FCSTD DOCUMENT  (FreeCAD 1.0R38643 (Git))
Label: Acryl03
License: All rights reserved
LicenseURL: https://en.wikipedia.org/wiki/All_rights_reserved
objects: Sketcher::SketchObject×1, PartDesign::Body×1
note: 3 computed .brp shape members not serialized (recipe doc carries the construction recipe); baked Part::Feature solids carry a one-line shape summary decoded from their .brp

FEATURE [Sketcher::SketchObject] Sketch
  ArcFitTolerance = 1e-06
  AttachmentSupport = -> [XY_Plane]
  FullyConstrained = false
  MakeInternals = false
  MapMode = 5
  sketch-geometry (64):
    g0: LineSegment StartX=-152.327 StartY=63 StartZ=0 EndX=-152.327 EndY=44.1 EndZ=0
    g1: LineSegment StartX=-140.327 StartY=3.12586e-11 StartZ=0 EndX=-108.827 EndY=3.12586e-11 EndZ=0
    g2: LineSegment StartX=5.67322 StartY=74.9996 StartZ=0 EndX=-25.8266 EndY=74.9996 EndZ=0
    g3: ArcOfCircle CenterX=-140.327 CenterY=63 CenterZ=0 NormalX=0 NormalY=0 NormalZ=1 AngleXU=0 Radius=12 StartAngle=1.5708 EndAngle=3.14159
    g4: ArcOfCircle CenterX=-140.327 CenterY=12 CenterZ=0 NormalX=0 NormalY=0 NormalZ=1 AngleXU=0 Radius=12 StartAngle=3.14159 EndAngle=4.71239
    g5: ArcOfCircle CenterX=5.85959 CenterY=12 CenterZ=0 NormalX=0 NormalY=0 NormalZ=1 AngleXU=0 Radius=12 StartAngle=4.71242 EndAngle=6.28319
    g6: ArcOfCircle CenterX=5.67322 CenterY=62.9996 CenterZ=0 NormalX=0 NormalY=0 NormalZ=1 AngleXU=0 Radius=12 StartAngle=3.18953e-05 EndAngle=1.5708
    g7: GeomPoint [constr] X=-152.327 Y=75 Z=0
    g8: GeomPoint [constr] X=17.8605 Y=0 Z=0
    g9: Circle CenterX=5.96219 CenterY=55.25 CenterZ=0 NormalX=0 NormalY=0 NormalZ=1 AngleXU=0 Radius=1.1
    g10: Circle CenterX=-65.0378 CenterY=55.25 CenterZ=0 NormalX=0 NormalY=0 NormalZ=1 AngleXU=0 Radius=1.1
    g11: Circle CenterX=-65.0378 CenterY=19.75 CenterZ=0 NormalX=0 NormalY=0 NormalZ=1 AngleXU=0 Radius=1.1
    g12: Circle CenterX=5.96219 CenterY=19.75 CenterZ=0 NormalX=0 NormalY=0 NormalZ=1 AngleXU=0 Radius=1.1
    g13: ArcOfCircle CenterX=-12.1395 CenterY=37.5 CenterZ=0 NormalX=0 NormalY=0 NormalZ=1 AngleXU=0 Radius=12 StartAngle=1.5708 EndAngle=4.71239
    g14: LineSegment StartX=17.8605 StartY=25.5 StartZ=0 EndX=-12.1395 EndY=25.5 EndZ=0
    g15: LineSegment StartX=17.8605 StartY=49.5 StartZ=0 EndX=-12.1395 EndY=49.5 EndZ=0
    g16: LineSegment [constr] StartX=-65.0378 StartY=55.25 StartZ=0 EndX=-65.0378 EndY=19.75 EndZ=0
    g17: GeomPoint X=17.8605 Y=49.5 Z=0
    g18: GeomPoint X=17.8605 Y=25.5 Z=0
    g19: LineSegment StartX=17.8605 StartY=25.5 StartZ=0 EndX=17.8605 EndY=12 EndZ=0
    g20: LineSegment StartX=17.8605 StartY=49.5 StartZ=0 EndX=17.8605 EndY=63 EndZ=0
    g21: Circle CenterX=-140.327 CenterY=63 CenterZ=0 NormalX=0 NormalY=0 NormalZ=1 AngleXU=0 Radius=1.1
    g22: Circle CenterX=-140.327 CenterY=12 CenterZ=0 NormalX=0 NormalY=0 NormalZ=1 AngleXU=0 Radius=1.1
    g23: Circle CenterX=5.85959 CenterY=12 CenterZ=0 NormalX=0 NormalY=0 NormalZ=1 AngleXU=0 Radius=1.1
    g24: Circle CenterX=5.67322 CenterY=62.9996 CenterZ=0 NormalX=0 NormalY=0 NormalZ=1 AngleXU=0 Radius=1.1
    g25: LineSegment [constr] StartX=-115.261 StartY=75 StartZ=0 EndX=-115.261 EndY=4.69e-13 EndZ=0
    g26: GeomPoint X=-115.261 Y=37.5 Z=0
    g27: Circle CenterX=-115.261 CenterY=37.5 CenterZ=0 NormalX=0 NormalY=0 NormalZ=1 AngleXU=0 Radius=3.75
    g28: Circle CenterX=-115.261 CenterY=56.25 CenterZ=0 NormalX=0 NormalY=0 NormalZ=1 AngleXU=0 Radius=3.75
    g29: LineSegment [constr] StartX=-110.295 StartY=75 StartZ=0 EndX=-110.295 EndY=37.5 EndZ=0
    g30: GeomPoint X=-110.295 Y=56.25 Z=0
    g31: LineSegment [constr] StartX=-110.295 StartY=56.25 StartZ=0 EndX=-152.327 EndY=56.25 EndZ=0
    g32: GeomPoint X=-115.261 Y=56.25 Z=0
    g33: Circle CenterX=-115.261 CenterY=18.75 CenterZ=0 NormalX=0 NormalY=0 NormalZ=1 AngleXU=0 Radius=3.75
    g34: GeomPoint X=-115.261 Y=18.75 Z=0
    g35: LineSegment StartX=-108.827 StartY=71 StartZ=0 EndX=-98.8266 EndY=71 EndZ=0
    g36: LineSegment StartX=-72.3266 StartY=71 StartZ=0 EndX=-62.3266 EndY=71 EndZ=0
    g37: LineSegment StartX=-62.3266 StartY=71 StartZ=0 EndX=-62.3266 EndY=75 EndZ=0
    g38: LineSegment StartX=-72.3266 StartY=75 StartZ=0 EndX=-72.3266 EndY=71 EndZ=0
    g39: LineSegment StartX=-35.8266 StartY=71 StartZ=0 EndX=-25.8266 EndY=71 EndZ=0
    g40: LineSegment StartX=-25.8266 StartY=71 StartZ=0 EndX=-25.8266 EndY=74.9996 EndZ=0
    g41: LineSegment StartX=-35.8266 StartY=75 StartZ=0 EndX=-35.8266 EndY=71 EndZ=0
    g42: GeomPoint X=-108.827 Y=75 Z=0
    g43: LineSegment StartX=-108.827 StartY=75 StartZ=0 EndX=-108.827 EndY=71 EndZ=0
    g44: LineSegment StartX=-98.8266 StartY=71 StartZ=0 EndX=-98.8266 EndY=75 EndZ=0
    g45: LineSegment StartX=-108.827 StartY=75 StartZ=0 EndX=-140.327 EndY=75 EndZ=0
    g46: LineSegment StartX=-72.3266 StartY=75 StartZ=0 EndX=-98.8266 EndY=75 EndZ=0
    g47: LineSegment StartX=-35.8266 StartY=75 StartZ=0 EndX=-62.3266 EndY=75 EndZ=0
    g48: LineSegment StartX=-98.8266 StartY=0 StartZ=0 EndX=-98.8266 EndY=4 EndZ=0
    g49: LineSegment StartX=-98.8266 StartY=4 StartZ=0 EndX=-108.827 EndY=4 EndZ=0
    g50: LineSegment StartX=-108.827 StartY=4 StartZ=0 EndX=-108.827 EndY=3.12586e-11 EndZ=0
    g51: LineSegment StartX=-62.2333 StartY=0 StartZ=0 EndX=-62.2333 EndY=4 EndZ=0
    g52: LineSegment StartX=-62.2333 StartY=4 StartZ=0 EndX=-72.2333 EndY=4 EndZ=0
    g53: LineSegment StartX=-72.2333 StartY=4 StartZ=0 EndX=-72.2333 EndY=0 EndZ=0
    g54: LineSegment StartX=-25.8266 StartY=0 StartZ=0 EndX=-25.8266 EndY=4 EndZ=0
    g55: LineSegment StartX=-25.8266 StartY=4 StartZ=0 EndX=-35.8266 EndY=4 EndZ=0
    g56: LineSegment StartX=-35.8266 StartY=4 StartZ=0 EndX=-35.8266 EndY=4e-16 EndZ=0
    g57: LineSegment StartX=-62.2333 StartY=0 StartZ=0 EndX=-35.8266 EndY=5e-16 EndZ=0
    g58: LineSegment StartX=-98.8266 StartY=0 StartZ=0 EndX=-72.2333 EndY=0 EndZ=0
    g59: LineSegment StartX=-25.8266 StartY=0 StartZ=0 EndX=5.85995 EndY=5.3e-15 EndZ=0
    g60: LineSegment StartX=-152.327 StartY=30.9 StartZ=0 EndX=-127.327 EndY=30.9 EndZ=0
    g61: LineSegment StartX=-127.327 StartY=30.9 StartZ=0 EndX=-127.327 EndY=44.1 EndZ=0
    g62: LineSegment StartX=-127.327 StartY=44.1 StartZ=0 EndX=-152.327 EndY=44.1 EndZ=0
    g63: LineSegment StartX=-152.327 StartY=30.9 StartZ=0 EndX=-152.327 EndY=12 EndZ=0
  constraints (129):
    c: Tangent(g0,g3) = -1.5708
    c: Coincident(g63,g4) = -1.5708
    c: Tangent(g1,g4) = -1.5708
    c: Coincident(g59,g5) = -1.5708
    c: Tangent(g2,g6) = -1.5708
    c: Coincident(g45,g3) = -1.5708
    c: Vertical(g0)
    c: Horizontal(g1)
    c: Horizontal(g2)
    c: Equal(g3,g4)
    c: Equal(g4,g5)
    c: Equal(g5,g6)
    c: PointOnObject(g7,g0)
    c: PointOnObject(g7,g45)
    c: PointOnObject(g8,g59)
    c: Distance(g0,g6) = 170
    c: Distance(g1,g45) = 75
    c: Radius(g4) = 12
    c: PointOnObject(g8,g-1)
    c: Diameter(g9) = 2.2
    c: Diameter(g10) = 2.2
    c: Horizontal(g9,g10)
    c: DistanceX(g10,g9) = 71
    c: Diameter(g11) = 2.2
    c: Diameter(g12) = 2.2
    c: Vertical(g11,g10)
    c: Vertical(g12,g9)
    c: Horizontal(g11,g12)
    c: DistanceY(g11,g10) = 35.5
    c: Tangent(g13,g14) = 1.5708
    c: Tangent(g13,g15) = -1.5708
    c: Angle(g-1,g14) = 3.14159
    c: Coincident(g16,g10)
    c: Coincident(g16,g11)
    c: Coincident(g17,g15)
    c: Coincident(g18,g14)
    c: Coincident(g19,g14)
    c: Vertical(g19)
    c: Coincident(g20,g15)
    c: Vertical(g20)
    c: Diameter(g21) = 2.2
    c: Coincident(g21,g3)
    c: Diameter(g22) = 2.2
    c: Coincident(g22,g4)
    c: Diameter(g23) = 2.2
    c: Coincident(g23,g5)
    c: Diameter(g24) = 2.2
    c: Coincident(g24,g6)
    c: PointOnObject(g25,g45)
    c: PointOnObject(g25,g1)
    c: Vertical(g25)
    c: Symmetric(g25,g25,g26)
    c: Diameter(g27) = 7.5
    c: Coincident(g27,g26)
    c: Diameter(g28) = 7.5
    c: PointOnObject(g29,g45)
    c: Vertical(g29)
    c: Symmetric(g29,g29,g30)
    c: Coincident(g31,g30)
    c: PointOnObject(g31,g0)
    c: Horizontal(g31)
    c: DistanceY(g26,g25) = 37.5
    c: PointOnObject(g32,g25)
    c: DistanceY(g32,g25) = 18.75
    c: Coincident(g28,g32)
    c: Diameter(g33) = 7.5
    c: PointOnObject(g34,g25)
    c: DistanceY(g25,g34) = 18.75
    c: Coincident(g34,g33)
    c: Horizontal(g35)
    c: Distance(g35,g35) = 10
    c: Coincident(g36,g37)
    c: Coincident(g38,g36)
    c: Horizontal(g36)
    c: Vertical(g37)
    c: Vertical(g38)
    c: Distance(g37,g38) = 10
    c: Coincident(g39,g40)
    c: Coincident(g41,g39)
    c: Horizontal(g39)
    c: Vertical(g40)
    c: Vertical(g41)
    c: Distance(g40,g41) = 10
    c: Coincident(g43,g42)
    c: Coincident(g43,g35)
    c: Vertical(g43)
    c: Coincident(g44,g35)
    c: Vertical(g44)
    c: Coincident(g46,g44)
    c: PointOnObject(g45,g43)
    c: PointOnObject(g38,g46)
    c: Coincident(g47,g37)
    c: PointOnObject(g46,g38)
    c: PointOnObject(g41,g47)
    c: Coincident(g2,g40)
    c: PointOnObject(g47,g41)
    c: Coincident(g48,g49)
    c: Coincident(g49,g50)
    c: Horizontal(g49)
    c: Vertical(g48)
    c: Vertical(g50)
    c: Coincident(g51,g52)
    c: Coincident(g52,g53)
    c: Horizontal(g52)
    c: Vertical(g51)
    c: Vertical(g53)
    c: Coincident(g54,g55)
    c: Coincident(g55,g56)
    c: Horizontal(g55)
    c: Vertical(g54)
    c: Vertical(g56)
    c: PointOnObject(g48,g58)
    c: PointOnObject(g51,g57)
    c: Coincident(g58,g53)
    c: PointOnObject(g57,g51)
    c: Coincident(g1,g50)
    c: PointOnObject(g58,g48)
    c: Coincident(g57,g56)
    c: Coincident(g54,g59)
    c: Coincident(g60,g61)
    c: Coincident(g61,g62)
    c: Horizontal(g60)
    c: Horizontal(g62)
    c: Vertical(g61)
    c: Distance(g61,g60) = 25
    c: Distance(g60,g62) = 13.2
    c: Vertical(g62,g31)
    c: PointOnObject(g0,g62)
    c: PointOnObject(g63,g60)
FEATURE [PartDesign::Body] Body
  AllowCompound = false
  Group = -> [Sketch]
  Origin = -> Origin
